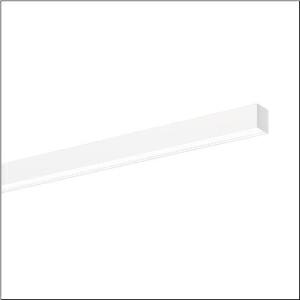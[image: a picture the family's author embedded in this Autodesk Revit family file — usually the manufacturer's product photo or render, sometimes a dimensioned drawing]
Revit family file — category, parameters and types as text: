
# Revit family: silica_21_51mx23da44wb
name_source: partatom
category: Lighting Fixtures
units: mm (PartAtom-declared; Revit-internal decimal feet)

## family parameters
Cut with Voids When Loaded = No
Host = Face
Light Source = No
Part Type = Normal
Room Calculation Point = No
Round Connector Dimension = Use Diameter
Shared = No

## types (1)
- --- (1 x LED, 3280 lm, 22.4 W, 4000K)
    Apparent Load = 22 VA
    CIE Flux Codes = 78 96 99 100 100
    Color Rendering = 80
    Color Temperature = 4000K
    Default Elevation = 1800 mm
    Description = Silica 21, office luminaire, primary optical cover: prismatic diffuser, of PMMA, CAT 2 (L<= 3000cd/m²), light emission: direct distribution, primary light characteristic: symmetric, installation type: surface-mounted, LED, rated luminous flux: 3.280lm, luminous efficacy: 146lm/W, light colour: 840, colour temperature: 4000K, control gear: DALI 2, with terminal, 3+2-pole, max. 2.5mm², mains connection: 220..240V, AC, 50/60Hz, rated input power: 22.4W, luminaire housing, of aluminium, traffic white (RAL 9016), length: 1.204mm, width: 53mm, height: 53mm, protection rating (complete): IP20, insulation class (complete): insulation class I (protective earthing), certification: CE, permissible operating ambient temperature: 0..+35°C, standard: EN 50419, packaging unit: 1 piece
    Height = 53 mm
    Lamp = 1 x LED
    Lamp Light Flux = 3280 lm
    Lamp Power = 22.4 W
    Lamp count = 1
    Length = 1204 mm
    Luminous efficacy = 146 lm/W
    Manufacturer = Siteco
    ModVariant = No
    Model = 51MX23DA44WB
    Mounting Place = Ceiling
    Mounting Type = Surface mounted
    Number of Poles = 1
    OnlyDefault = Yes
    Power Factor = 1
    Product Name = Silica 21
    Product group = office luminaire | ceiling mounted
    ProductGroupID = 301
    Protection Class = Protection class I
    Protection Degree = IP 20
    RLX_Detail_Level = 1
    RLX_Emergency_Light_Flux = 0 lm
    RLX_Emergency_Type = 0
    RLX_Emergency_Type_DB = No
    RlxData = <blob elided: 18765 chars, md5=a992d394>
    Socket = socket
    Standby Power = 0 W
    System Light Flux = 3280 lm
    System Power = 22 W
    Type Comments = factory setting: luminous flux: 100 % | dim-lin: 254 | 323 mA
    Type Image = l_1335877.jpg
    URL = http://relux.com
    VarID = @adj_029849
    Voltage = 0 V
    Weight = 0.00 kg
    Width = 53 mm

## geometry (parser evidence)
native form markers: Blend x4, Sweep x12
no freeform markers — native parametric forms only
